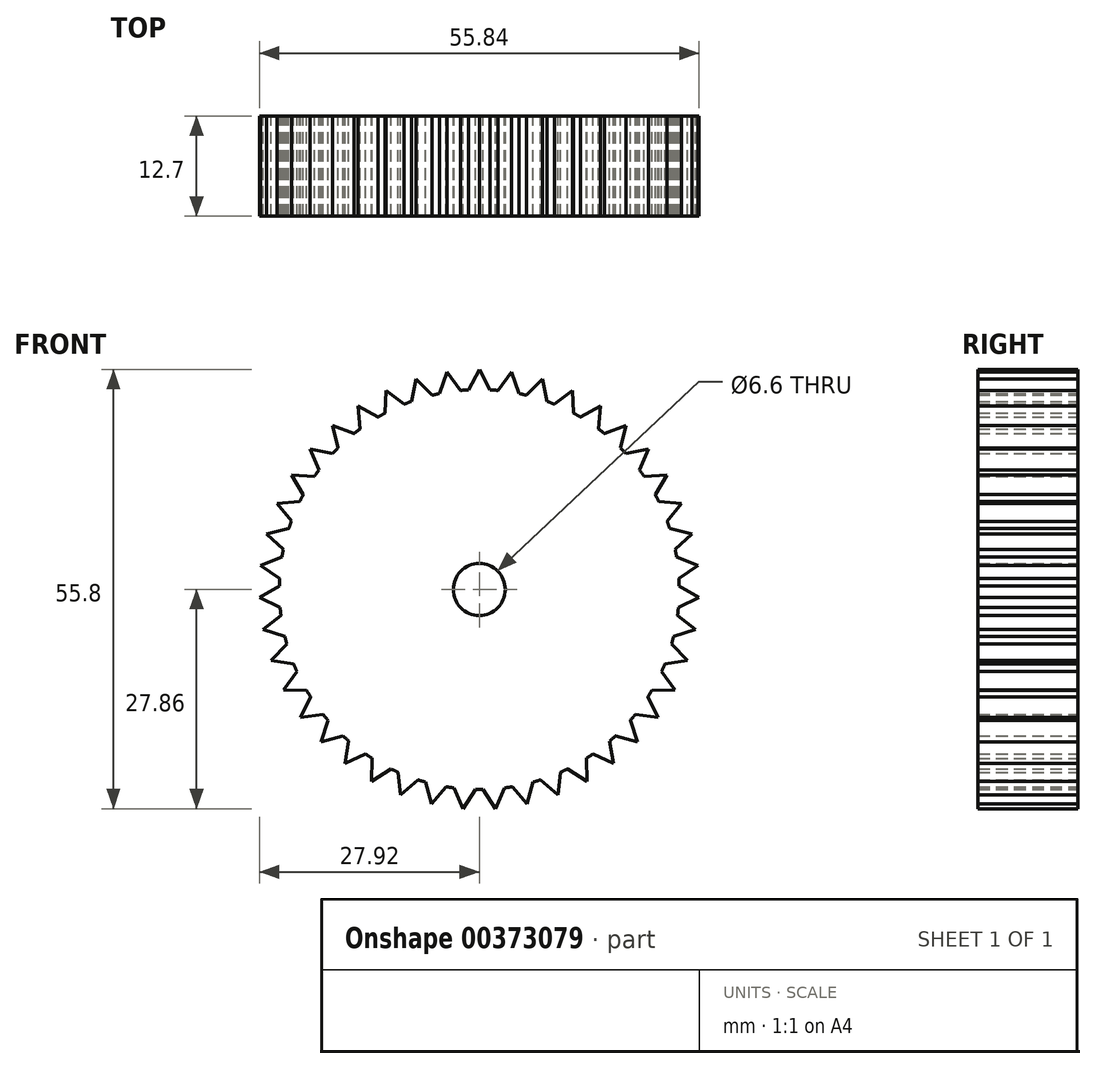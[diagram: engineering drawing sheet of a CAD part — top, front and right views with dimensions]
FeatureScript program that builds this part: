
annotation { "Feature Type Name" : "Feature", "Feature Type Description" : "" }
export const myFeature = defineFeature(function(context is Context, id is Id, definition is map)
    precondition{}
    {
        {
            var Q0;
            Q0=qCreatedBy(makeId("Front.planeOp"),FACE);
            var sketch = newSketch(context, id + "F0", { "sketchPlane" : qUnion([Q0])});
            skCircle(sketch, "E0", {"center": v(0, 0) * mm, "radius": 25.4 * mm});
            skCircle(sketch, "E1", {"center": v(0, 0) * mm, "radius": 3.3 * mm});
            skLineSegment(sketch, "E2", {"start": v(0, 27.94) * mm, "end": v(-1.35, 25.36) * mm});
            skLineSegment(sketch, "E3", {"start": v(0, 27.94) * mm, "end": v(1.36, 25.36) * mm});
            skLineSegment(sketch, "E4", {"start": v(1.36, 25.36) * mm, "end": v(0, 25.4) * mm});
            skLineSegment(sketch, "E5.1.2", {"start": v(-4.07, 27.64) * mm, "end": v(-2.35, 25.3) * mm});
            skLineSegment(sketch, "E5.1.3", {"start": v(-4.07, 27.64) * mm, "end": v(-5.03, 24.9) * mm});
            skLineSegment(sketch, "E5.2.2", {"start": v(-8.05, 26.75) * mm, "end": v(-6, 24.68) * mm});
            skLineSegment(sketch, "E5.2.3", {"start": v(-8.05, 26.75) * mm, "end": v(-8.6, 23.9) * mm});
            skLineSegment(sketch, "E5.3.2", {"start": v(-11.86, 25.3) * mm, "end": v(-9.54, 23.54) * mm});
            skLineSegment(sketch, "E5.3.3", {"start": v(-11.86, 25.3) * mm, "end": v(-11.99, 22.4) * mm});
            skLineSegment(sketch, "E5.4.2", {"start": v(-15.41, 23.3) * mm, "end": v(-12.86, 21.9) * mm});
            skLineSegment(sketch, "E5.4.3", {"start": v(-15.41, 23.3) * mm, "end": v(-15.12, 20.4) * mm});
            skLineSegment(sketch, "E5.5.2", {"start": v(-18.64, 20.8) * mm, "end": v(-15.92, 19.8) * mm});
            skLineSegment(sketch, "E5.5.3", {"start": v(-18.64, 20.8) * mm, "end": v(-17.93, 17.99) * mm});
            skLineSegment(sketch, "E5.6.2", {"start": v(-21.47, 17.87) * mm, "end": v(-18.63, 17.27) * mm});
            skLineSegment(sketch, "E5.6.3", {"start": v(-21.47, 17.87) * mm, "end": v(-20.36, 15.19) * mm});
            skLineSegment(sketch, "E5.7.2", {"start": v(-23.85, 14.55) * mm, "end": v(-20.94, 14.37) * mm});
            skLineSegment(sketch, "E5.7.3", {"start": v(-23.85, 14.55) * mm, "end": v(-22.35, 12.06) * mm});
            skLineSegment(sketch, "E5.8.2", {"start": v(-25.71, 10.93) * mm, "end": v(-22.81, 11.17) * mm});
            skLineSegment(sketch, "E5.8.3", {"start": v(-25.71, 10.93) * mm, "end": v(-23.87, 8.68) * mm});
            skLineSegment(sketch, "E5.9.2", {"start": v(-27.03, 7.07) * mm, "end": v(-24.2, 7.73) * mm});
            skLineSegment(sketch, "E5.9.3", {"start": v(-27.03, 7.07) * mm, "end": v(-24.88, 5.1) * mm});
            skLineSegment(sketch, "E5.10.2", {"start": v(-27.77, 3.06) * mm, "end": v(-25.06, 4.12) * mm});
            skLineSegment(sketch, "E5.10.3", {"start": v(-27.77, 3.06) * mm, "end": v(-25.36, 1.43) * mm});
            skLineSegment(sketch, "E5.11.2", {"start": v(-27.92, -1.02) * mm, "end": v(-25.4, 0.43) * mm});
            skLineSegment(sketch, "E5.11.3", {"start": v(-27.92, -1.02) * mm, "end": v(-25.3, -2.28) * mm});
            skLineSegment(sketch, "E5.12.2", {"start": v(-27.47, -5.07) * mm, "end": v(-25.19, -3.27) * mm});
            skLineSegment(sketch, "E5.12.3", {"start": v(-27.47, -5.07) * mm, "end": v(-24.7, -5.93) * mm});
            skLineSegment(sketch, "E5.13.2", {"start": v(-26.44, -9.02) * mm, "end": v(-24.44, -6.9) * mm});
            skLineSegment(sketch, "E5.13.3", {"start": v(-26.44, -9.02) * mm, "end": v(-23.57, -9.47) * mm});
            skLineSegment(sketch, "E5.14.2", {"start": v(-24.84, -12.77) * mm, "end": v(-23.18, -10.4) * mm});
            skLineSegment(sketch, "E5.14.3", {"start": v(-24.84, -12.77) * mm, "end": v(-21.94, -12.8) * mm});
            skLineSegment(sketch, "E5.15.2", {"start": v(-22.72, -16.25) * mm, "end": v(-21.42, -13.66) * mm});
            skLineSegment(sketch, "E5.15.3", {"start": v(-22.72, -16.25) * mm, "end": v(-19.84, -15.86) * mm});
            skLineSegment(sketch, "E5.16.2", {"start": v(-20.11, -19.39) * mm, "end": v(-19.2, -16.63) * mm});
            skLineSegment(sketch, "E5.16.3", {"start": v(-20.11, -19.39) * mm, "end": v(-17.32, -18.58) * mm});
            skLineSegment(sketch, "E5.17.2", {"start": v(-17.07, -22.11) * mm, "end": v(-16.57, -19.25) * mm});
            skLineSegment(sketch, "E5.17.3", {"start": v(-17.07, -22.11) * mm, "end": v(-14.43, -20.9) * mm});
            skLineSegment(sketch, "E5.18.2", {"start": v(-13.67, -24.36) * mm, "end": v(-13.6, -21.46) * mm});
            skLineSegment(sketch, "E5.18.3", {"start": v(-13.67, -24.36) * mm, "end": v(-11.24, -22.78) * mm});
            skLineSegment(sketch, "E5.19.2", {"start": v(-9.98, -26.1) * mm, "end": v(-10.33, -23.2) * mm});
            skLineSegment(sketch, "E5.19.3", {"start": v(-9.98, -26.1) * mm, "end": v(-7.8, -24.17) * mm});
            skLineSegment(sketch, "E5.20.2", {"start": v(-6.07, -27.27) * mm, "end": v(-6.84, -24.46) * mm});
            skLineSegment(sketch, "E5.20.3", {"start": v(-6.07, -27.27) * mm, "end": v(-4.2, -25.05) * mm});
            skLineSegment(sketch, "E5.21.2", {"start": v(-2.04, -27.86) * mm, "end": v(-3.2, -25.2) * mm});
            skLineSegment(sketch, "E5.21.3", {"start": v(-2.04, -27.86) * mm, "end": v(-0.5, -25.4) * mm});
            skLineSegment(sketch, "E5.22.2", {"start": v(2.04, -27.86) * mm, "end": v(0.5, -25.4) * mm});
            skLineSegment(sketch, "E5.22.3", {"start": v(2.04, -27.86) * mm, "end": v(3.2, -25.2) * mm});
            skLineSegment(sketch, "E5.23.2", {"start": v(6.07, -27.27) * mm, "end": v(4.2, -25.05) * mm});
            skLineSegment(sketch, "E5.23.3", {"start": v(6.07, -27.27) * mm, "end": v(6.83, -24.46) * mm});
            skLineSegment(sketch, "E5.24.2", {"start": v(9.98, -26.1) * mm, "end": v(7.8, -24.17) * mm});
            skLineSegment(sketch, "E5.24.3", {"start": v(9.98, -26.1) * mm, "end": v(10.32, -23.2) * mm});
            skLineSegment(sketch, "E5.25.2", {"start": v(13.67, -24.36) * mm, "end": v(11.23, -22.78) * mm});
            skLineSegment(sketch, "E5.25.3", {"start": v(13.67, -24.36) * mm, "end": v(13.6, -21.46) * mm});
            skLineSegment(sketch, "E5.26.2", {"start": v(17.07, -22.11) * mm, "end": v(14.43, -20.9) * mm});
            skLineSegment(sketch, "E5.26.3", {"start": v(17.07, -22.11) * mm, "end": v(16.57, -19.25) * mm});
            skLineSegment(sketch, "E5.27.2", {"start": v(20.11, -19.39) * mm, "end": v(17.32, -18.58) * mm});
            skLineSegment(sketch, "E5.27.3", {"start": v(20.11, -19.39) * mm, "end": v(19.2, -16.63) * mm});
            skLineSegment(sketch, "E5.28.2", {"start": v(22.72, -16.25) * mm, "end": v(19.84, -15.86) * mm});
            skLineSegment(sketch, "E5.28.3", {"start": v(22.72, -16.25) * mm, "end": v(21.41, -13.66) * mm});
            skLineSegment(sketch, "E5.29.2", {"start": v(24.84, -12.77) * mm, "end": v(21.94, -12.8) * mm});
            skLineSegment(sketch, "E5.29.3", {"start": v(24.84, -12.77) * mm, "end": v(23.17, -10.4) * mm});
            skLineSegment(sketch, "E5.30.2", {"start": v(26.44, -9.02) * mm, "end": v(23.57, -9.47) * mm});
            skLineSegment(sketch, "E5.30.3", {"start": v(26.44, -9.02) * mm, "end": v(24.44, -6.91) * mm});
            skLineSegment(sketch, "E5.31.2", {"start": v(27.47, -5.07) * mm, "end": v(24.7, -5.94) * mm});
            skLineSegment(sketch, "E5.31.3", {"start": v(27.47, -5.07) * mm, "end": v(25.19, -3.28) * mm});
            skLineSegment(sketch, "E5.32.2", {"start": v(27.92, -1.02) * mm, "end": v(25.3, -2.28) * mm});
            skLineSegment(sketch, "E5.32.3", {"start": v(27.92, -1.02) * mm, "end": v(25.4, 0.42) * mm});
            skLineSegment(sketch, "E5.33.2", {"start": v(27.77, 3.06) * mm, "end": v(25.36, 1.43) * mm});
            skLineSegment(sketch, "E5.33.3", {"start": v(27.77, 3.06) * mm, "end": v(25.06, 4.12) * mm});
            skLineSegment(sketch, "E5.34.2", {"start": v(27.03, 7.07) * mm, "end": v(24.88, 5.1) * mm});
            skLineSegment(sketch, "E5.34.3", {"start": v(27.03, 7.07) * mm, "end": v(24.2, 7.72) * mm});
            skLineSegment(sketch, "E5.35.2", {"start": v(25.71, 10.93) * mm, "end": v(23.87, 8.67) * mm});
            skLineSegment(sketch, "E5.35.3", {"start": v(25.71, 10.93) * mm, "end": v(22.82, 11.16) * mm});
            skLineSegment(sketch, "E5.36.2", {"start": v(23.85, 14.55) * mm, "end": v(22.36, 12.06) * mm});
            skLineSegment(sketch, "E5.36.3", {"start": v(23.85, 14.55) * mm, "end": v(20.95, 14.37) * mm});
            skLineSegment(sketch, "E5.37.2", {"start": v(21.47, 17.87) * mm, "end": v(20.36, 15.18) * mm});
            skLineSegment(sketch, "E5.37.3", {"start": v(21.47, 17.87) * mm, "end": v(18.63, 17.26) * mm});
            skLineSegment(sketch, "E5.38.2", {"start": v(18.64, 20.8) * mm, "end": v(17.94, 17.99) * mm});
            skLineSegment(sketch, "E5.38.3", {"start": v(18.64, 20.8) * mm, "end": v(15.92, 19.8) * mm});
            skLineSegment(sketch, "E5.39.2", {"start": v(15.41, 23.3) * mm, "end": v(15.13, 20.4) * mm});
            skLineSegment(sketch, "E5.39.3", {"start": v(15.41, 23.3) * mm, "end": v(12.87, 21.9) * mm});
            skLineSegment(sketch, "E5.40.2", {"start": v(11.86, 25.3) * mm, "end": v(12, 22.4) * mm});
            skLineSegment(sketch, "E5.40.3", {"start": v(11.86, 25.3) * mm, "end": v(9.54, 23.54) * mm});
            skLineSegment(sketch, "E5.41.2", {"start": v(8.05, 26.75) * mm, "end": v(8.6, 23.9) * mm});
            skLineSegment(sketch, "E5.41.3", {"start": v(8.05, 26.75) * mm, "end": v(6.01, 24.68) * mm});
            skLineSegment(sketch, "E5.42.2", {"start": v(4.07, 27.64) * mm, "end": v(5.03, 24.9) * mm});
            skLineSegment(sketch, "E5.42.3", {"start": v(4.07, 27.64) * mm, "end": v(2.36, 25.3) * mm});
            skSolve(sketch);
        }
        {
            var Q0;
            Q0 = qSketchRegion(id + "F0", true);
            extrude(context, id + "F1", {"entities" : qUnion([Q0]), "depth" : 12.7 * mm});
        }
    });
